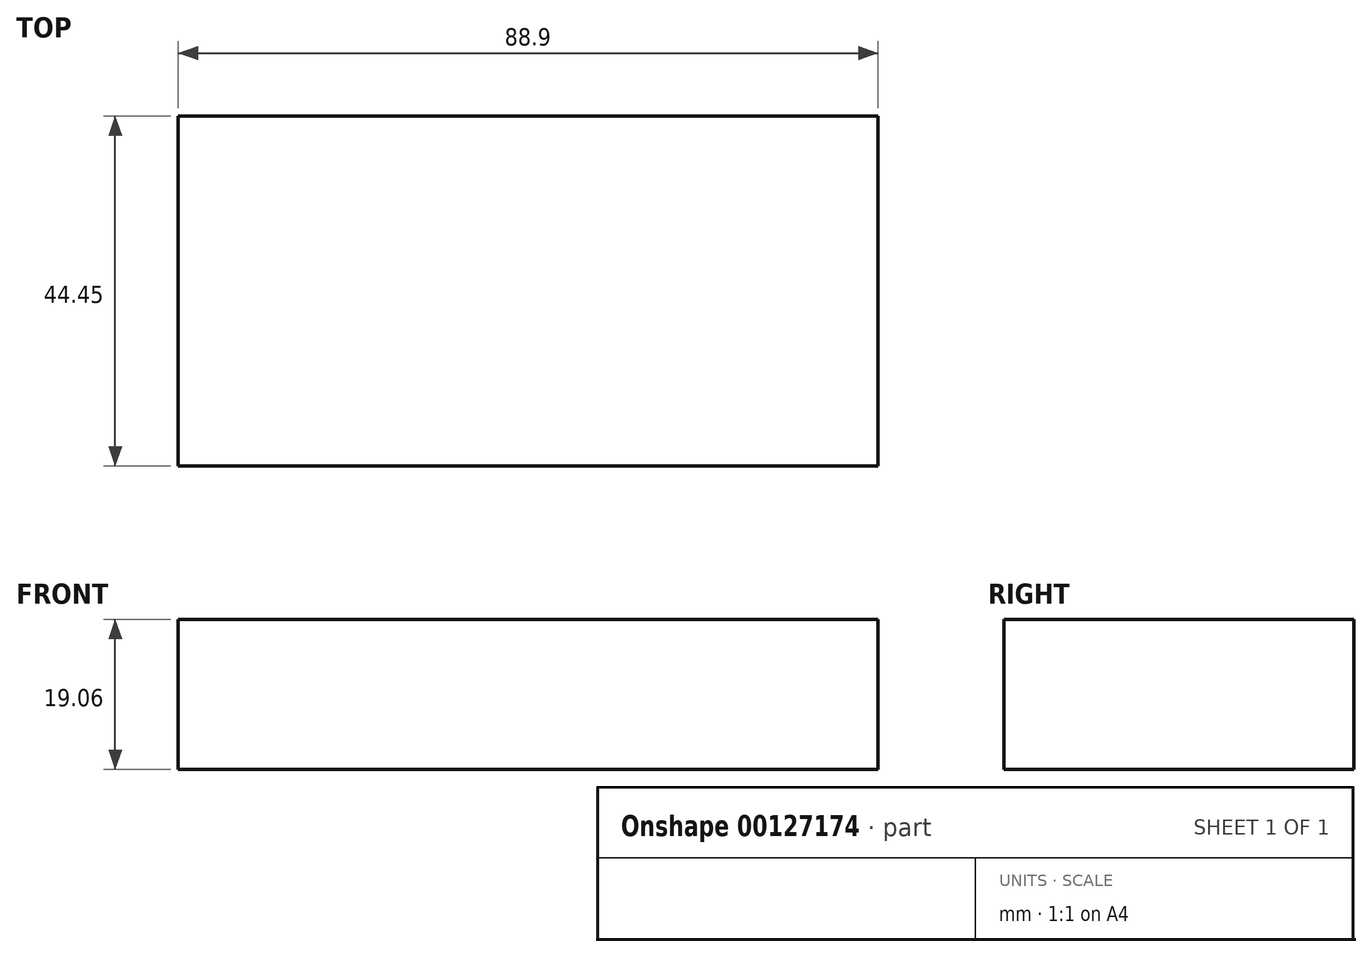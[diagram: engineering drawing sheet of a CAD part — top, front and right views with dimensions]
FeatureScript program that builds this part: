
annotation { "Feature Type Name" : "Feature", "Feature Type Description" : "" }
export const myFeature = defineFeature(function(context is Context, id is Id, definition is map)
    precondition{}
    {
        {
            var Q0;
            Q0=qCreatedBy(makeId("Front.planeOp"),FACE);
            var sketch = newSketch(context, id + "F0", { "sketchPlane" : qUnion([Q0])});
            skLineSegment(sketch, "E0.bottom", {"start": v(44.45, -9.52) * mm, "end": v(-44.45, -9.53) * mm});
            skLineSegment(sketch, "E0.top", {"start": v(44.45, 9.53) * mm, "end": v(-44.45, 9.53) * mm});
            skLineSegment(sketch, "E0.left", {"start": v(44.45, -9.52) * mm, "end": v(44.45, 9.53) * mm});
            skLineSegment(sketch, "E0.right", {"start": v(-44.45, -9.53) * mm, "end": v(-44.45, 9.53) * mm});
            skPoint(sketch, "E0.middle", {"position": v(0, 0) * mm});
            skSolve(sketch);
        }
        {
            var Q0;
            Q0=qSketchRegion(id+"F0",true);
            extrude(context, id + "F1", {"entities" : qUnion([Q0]), "depth" : 44.45 * mm});
        }
    });
